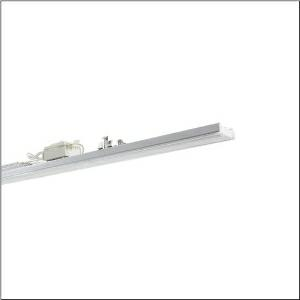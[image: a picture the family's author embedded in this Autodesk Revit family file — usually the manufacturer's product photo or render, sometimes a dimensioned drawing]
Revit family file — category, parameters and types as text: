
# Revit family: licross_r__11_recessed_mo_51tl187n485g_eb2d
name_source: partatom
category: Lighting Fixtures
units: mm (PartAtom-declared; Revit-internal decimal feet)

## family parameters
Cut with Voids When Loaded = No
Host = Face
Light Source = No
Part Type = Normal
Room Calculation Point = No
Round Connector Dimension = Use Diameter
Shared = No

## types (1)
- Licross® 11 Recessed MO (1 x LED, 8700 lm, 48.5 W, 4000K)
    Apparent Load = 49 VA
    CIE Flux Codes = 83 96 99 100 100
    Color Rendering = 80
    Color Temperature = 4000K
    Default Elevation = 1800 mm
    Description = Licross® 11 Recessed MO, luminaire insert, of sheet steel, coil coated, white, length: 1.500mm, width: 66mm, height: 67mm, LED rated luminous flux: 8.700lm, light colour: 840, control gear: ON/OFF, with plug, 3-pole, with phase selection, mains connection: 220..240V, AC, 50/60Hz, rated input power: 49W, internal wiring halogen-free, primary light control with lens, of plastic, primary optical cover: cover, of PMMA, light emission: direct distribution, primary light characteristic: symmetric, protection rating (complete): IP40, insulation class (complete): insulation class I (protective earthing), certification: CE, ENEC, VDE, UKCA, protection symbol: D if used in an environment without relevant dust loads with corresponding accessories, impact resistance: IK06, permissible ambient temperature for indoor applications: -35..+35°C, corresponds to IFS (International Featured Standards) requirements for safety and quality in the food industry, reducing of maximum allowable ambient temperature of 5°C with ceiling mounting, packaging unit: 1 piece
    Height = 58 mm
    Lamp = 1 x LED
    Lamp Light Flux = 8700 lm
    Lamp Power = 48.5 W
    Lamp count = 1
    Length = 1500 mm
    Luminous efficacy = 179 lm/W
    Manufacturer = Siteco
    ModVariant = No
    Model = 51TL187N485G
    Mounting Place = Ceiling
    Mounting Type = Pendant
    Number of Poles = 1
    OnlyDefault = Yes
    Power Factor = 1
    Product Name = Licross® 11 Recessed MO
    Product group = luminaire insert | ceiling pendant
    ProductGroupID = 902
    Protection Class = Protection class I
    Protection Degree = IP 40
    RLX_Detail_Level = 1
    RLX_Emergency_Light_Flux = 0 lm
    RLX_Emergency_Type = 0
    RLX_Emergency_Type_DB = No
    RlxData = <blob elided: 20773 chars, md5=bc920c6d>
    Socket = socket
    Standby Power = 0 W
    System Light Flux = 8700 lm
    System Power = 49 W
    Type Comments = Product without accessories
    Type Image = l_1296930.jpg
    URL = http://relux.com
    VarID = ---
    Voltage = 0 V
    Weight = 0.00 kg
    Width = 66 mm

## geometry (parser evidence)
native form markers: Blend x4, Sweep x11
no freeform markers — native parametric forms only
